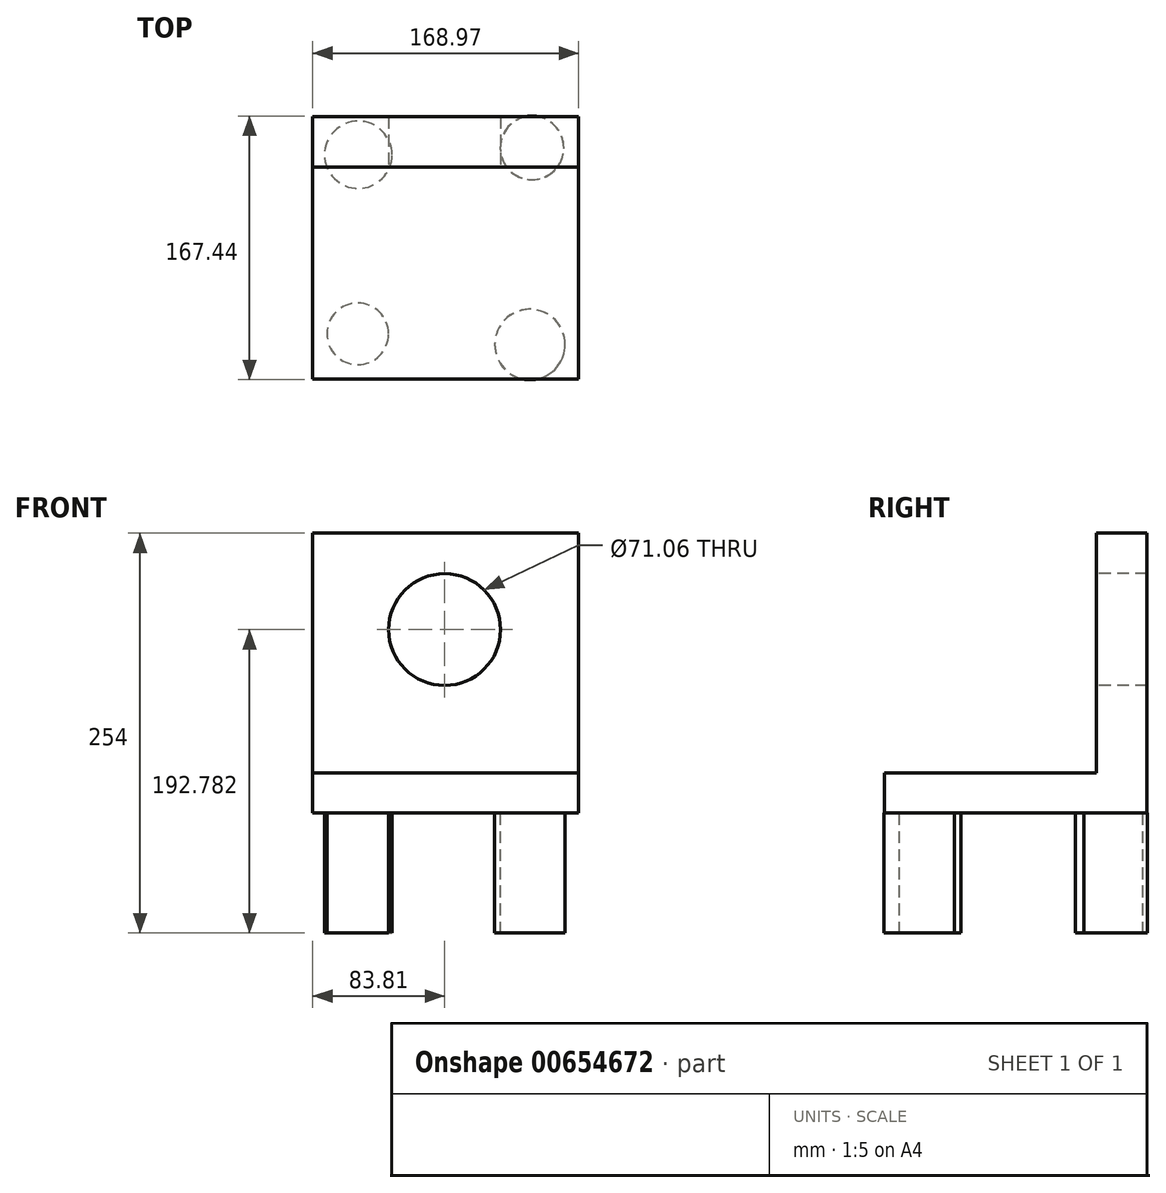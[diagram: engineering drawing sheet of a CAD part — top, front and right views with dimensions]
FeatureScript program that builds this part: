
annotation { "Feature Type Name" : "Feature", "Feature Type Description" : "" }
export const myFeature = defineFeature(function(context is Context, id is Id, definition is map)
    precondition{}
    {
        {
            var Q0;
            Q0=qCreatedBy(makeId("Top.planeOp"),FACE);
            var sketch = newSketch(context, id + "F0", { "sketchPlane" : qUnion([Q0])});
            skCircle(sketch, "E0", {"center": v(54.21, -66.73) * mm, "radius": 22.37 * mm});
            skCircle(sketch, "E1", {"center": v(55.51, 58.14) * mm, "radius": 20.2 * mm});
            skCircle(sketch, "E2", {"center": v(-54.8, 53.75) * mm, "radius": 21.4 * mm});
            skCircle(sketch, "E3", {"center": v(-55.2, -59.94) * mm, "radius": 19.57 * mm});
            skSolve(sketch);
        }
        {
            var Q0;
            Q0 = qSketchRegion(id + "F0", true);
            extrude(context, id + "F1", {"entities" : qUnion([Q0]), "depth" : 76.2 * mm, "offsetDistance" : 25.4 * mm});
        }
        {
            var Q0;
            Q0=makeQuery(id+"F1.opExtrude","CAP_FACE",FACE,{"disambiguationData":[OSD([sQuery(id+"F0.wireOp",EDGE,"E1")])],"isStart":false});
            var sketch = newSketch(context, id + "F2", { "sketchPlane" : qUnion([Q0])});
            skLineSegment(sketch, "E4.bottom", {"start": v(-83.8, 78.01) * mm, "end": v(85.16, 78.01) * mm});
            skLineSegment(sketch, "E4.top", {"start": v(-83.8, -88.79) * mm, "end": v(85.16, -88.79) * mm});
            skLineSegment(sketch, "E4.left", {"start": v(-83.8, 78.01) * mm, "end": v(-83.8, -88.79) * mm});
            skLineSegment(sketch, "E4.right", {"start": v(85.16, 78.01) * mm, "end": v(85.16, -88.79) * mm});
            skSolve(sketch);
        }
        {
            var Q0;
            Q0 = qSketchRegion(id + "F2", true);
            extrude(context, id + "F3", {"entities" : qUnion([Q0]), "depth" : 25.4 * mm, "offsetDistance" : 25.4 * mm});
        }
        {
            var Q0;
            Q0=makeQuery(id+"F3.opExtrude","CAP_FACE",FACE,{"disambiguationData":[OSD([sQuery(id+"F2.wireOp",EDGE,"E4.bottom"),sQuery(id+"F2.wireOp",EDGE,"E4.top"),sQuery(id+"F2.wireOp",EDGE,"E4.left"),sQuery(id+"F2.wireOp",EDGE,"E4.right")])],"isStart":false});
            var sketch = newSketch(context, id + "F4", { "sketchPlane" : qUnion([Q0])});
            skLineSegment(sketch, "E5.bottom", {"start": v(-83.8, 78.01) * mm, "end": v(85.16, 78.01) * mm});
            skLineSegment(sketch, "E5.top", {"start": v(-83.8, 45.82) * mm, "end": v(85.16, 45.82) * mm});
            skLineSegment(sketch, "E5.left", {"start": v(-83.8, 78.01) * mm, "end": v(-83.8, 45.82) * mm});
            skLineSegment(sketch, "E5.right", {"start": v(85.16, 78.01) * mm, "end": v(85.16, 45.82) * mm});
            skSolve(sketch);
        }
        {
            var Q0;
            Q0 = qSketchRegion(id + "F4", true);
            extrude(context, id + "F5", {"entities" : qUnion([Q0]), "operationType" : NewBodyOperationType.ADD, "depth" : 152.4 * mm, "offsetDistance" : 25.4 * mm});
        }
        {
            var Q0;
            Q0=makeQuery(id+"F5.opExtrude","SWEPT_FACE",FACE,{"disambiguationData":[OSD([sQuery(id+"F4.wireOp",EDGE,"E5.top")])]});
            var sketch = newSketch(context, id + "F6", { "sketchPlane" : qUnion([Q0])});
            skCircle(sketch, "E6", {"center": v(0, 192.78) * mm, "radius": 35.53 * mm});
            skSolve(sketch);
        }
        {
            var Q0;
            Q0 = qSketchRegion(id + "F6", true);
            extrude(context, id + "F7", {"entities" : qUnion([Q0]), "operationType" : NewBodyOperationType.REMOVE, "oppositeDirection" : true, "depth" : 101.6 * mm, "offsetDistance" : 25.4 * mm});
        }
    });
